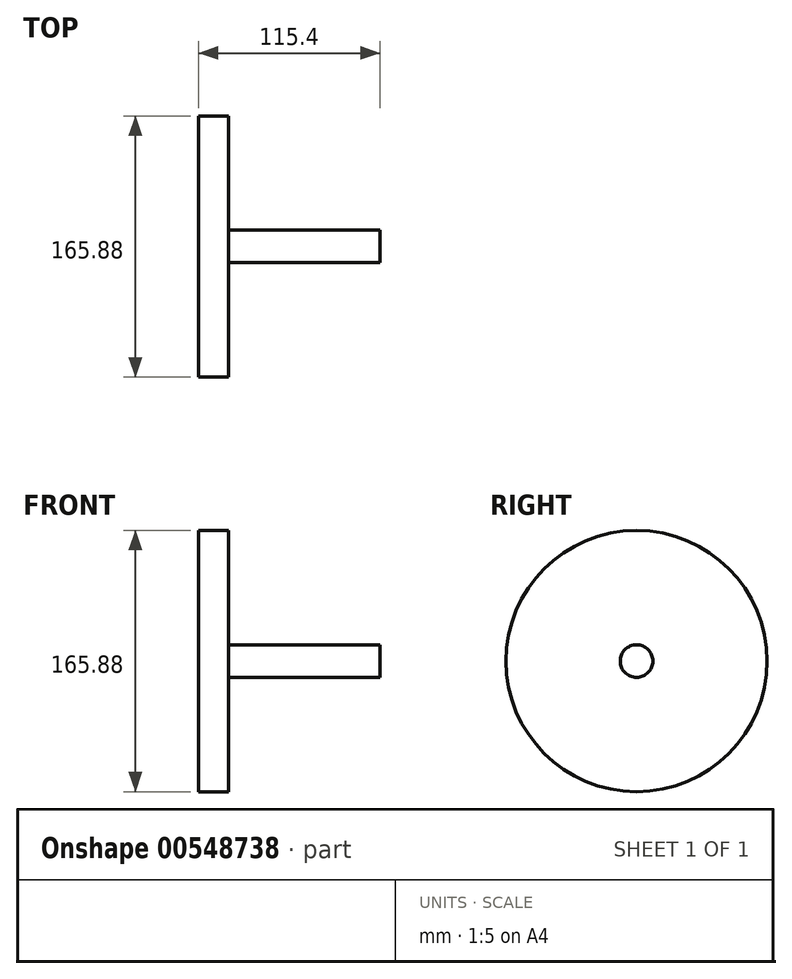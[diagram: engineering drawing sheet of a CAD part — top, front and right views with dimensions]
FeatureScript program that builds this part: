
annotation { "Feature Type Name" : "Feature", "Feature Type Description" : "" }
export const myFeature = defineFeature(function(context is Context, id is Id, definition is map)
    precondition{}
    {
        {
            var Q0;
            Q0=qCreatedBy(makeId("Front.planeOp"),FACE);
            var sketch = newSketch(context, id + "F0", { "sketchPlane" : qUnion([Q0])});
            skLineSegment(sketch, "E0", {"start": v(-50.87, 0) * mm, "end": v(0, 0) * mm, "construction": true});
            skLineSegment(sketch, "E1", {"start": v(-50.87, 82.94) * mm, "end": v(-50.87, 10.38) * mm});
            skLineSegment(sketch, "E2", {"start": v(-50.87, 10.38) * mm, "end": v(-31.69, 10.38) * mm});
            skLineSegment(sketch, "E3", {"start": v(-31.69, 10.38) * mm, "end": v(-31.69, 82.94) * mm});
            skLineSegment(sketch, "E4", {"start": v(-31.69, 82.94) * mm, "end": v(-50.87, 82.94) * mm});
            skLineSegment(sketch, "E5", {"start": v(-50.87, 10.38) * mm, "end": v(-50.87, 0) * mm});
            skLineSegment(sketch, "E6", {"start": v(-50.87, 0) * mm, "end": v(64.53, 0) * mm});
            skPoint(sketch, "E6.endSnap0", {"position": v(-25.43, 0) * mm});
            skLineSegment(sketch, "E7", {"start": v(64.53, 0) * mm, "end": v(64.53, 10.38) * mm});
            skLineSegment(sketch, "E8", {"start": v(64.53, 10.38) * mm, "end": v(-50.87, 10.38) * mm});
            skSolve(sketch);
        }
        {
            var Q0;
            {var subQ0=sQuery(id+"F0.wireOp",EDGE,"E1");Q0=makeQuery(id+"F0.imprint","IMPRINT",FACE,{"disambiguationData":[TD([[makeQuery(id+"F0.imprint","IMPRINT",EDGE,{"derivedFrom":subQ0}),1.0]])]});}
            var Q1;
            {var subQ3=sQuery(id+"F0.wireOp",EDGE,"E5");Q1=makeQuery(id+"F0.imprint","IMPRINT",FACE,{"disambiguationData":[TD([[makeQuery(id+"F0.imprint","IMPRINT",EDGE,{"derivedFrom":subQ3}),1.0]])]});}
            var Q2;
            Q2=sQuery(id+"F0.wireOp",EDGE,"E6");
            revolve(context, id + "F1", {"entities" : qUnion([Q0, Q1]), "axis" : qUnion([Q2]), "revolveType" : RevolveType.FULL});
        }
    });
